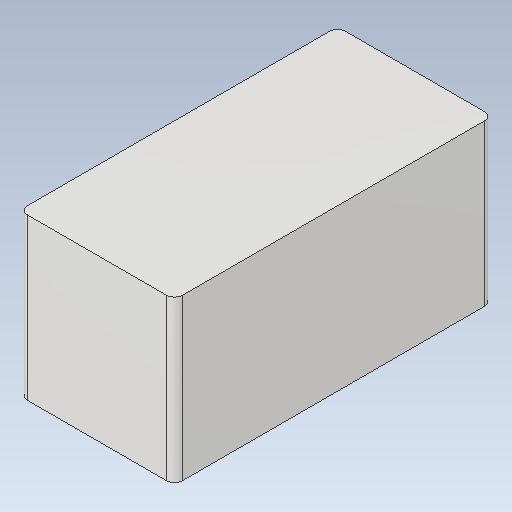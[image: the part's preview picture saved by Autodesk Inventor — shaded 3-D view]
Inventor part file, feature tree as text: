
AUTODESK INVENTOR PART (.ipt)
format: ipt  version: 2020 (Build 240168000, 168)  size: 92,160 bytes
history: native  units: mm
features: other x1, extrude x1, fillet x1, sketch x1
ambient origin geometry x8: Origin, YZ Plane, XZ Plane, XY Plane, X Axis, Y Axis, Z Axis, Center Point
bodies: Body1 (feature_tree)
feature tree (4):
  other  "Sólido1"
  extrude  "Extrusión1"  Depth=40.6mm
  fillet  "Empalme1"  Radius=20.5mm
  sketch  "Boceto1"  dims[d0=19.8mm d1=40.6mm d2=20.5mm d3=0.0mm d4=1.0mm]
